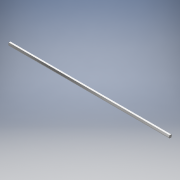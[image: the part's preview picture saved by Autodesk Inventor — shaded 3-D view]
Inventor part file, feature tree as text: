
AUTODESK INVENTOR PART (.ipt)
format: ipt  version: 2017 SP1 (Build 210196100, 196)  size: 101,888 bytes
history: native  units: in
note: dims shown in document units (in); Inventor stores cm internally (conversion verified against a paired STEP export)
features: extrude x1, sketch x1
ambient origin geometry x8: Origin, YZ Plane, XZ Plane, XY Plane, X Axis, Y Axis, Z Axis, Center Point
bodies: Solid1 (feature_tree)
feature tree (2):
  extrude  "Extrusion1"  Depth=0.375in
  sketch  "Sketch1"  dims[d1=21.75in d2=0.0in d3=0.375in d4=0.1in]
